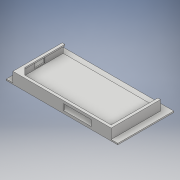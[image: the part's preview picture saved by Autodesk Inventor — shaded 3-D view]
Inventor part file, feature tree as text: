
AUTODESK INVENTOR PART (.ipt)
format: ipt  version: 2018 (Build 220112000, 112)  size: 165,888 bytes
history: native  units: mm
features: extrude x6, sketch x6, chamfer x1, projected_geometry x1
ambient origin geometry x8: Origin, YZ Plane, XZ Plane, XY Plane, X Axis, Y Axis, Z Axis, Center Point
bodies: Solid1 (feature_tree)
feature tree (14):
  extrude  "Extrusion1"  Depth=72.0mm
  extrude  "Extrusion2"  Depth=1.5mm
  extrude  "Extrusion3"  Depth=4.0mm
  extrude  "Extrusion4"  Depth=2.0mm TaperAngle=0.0deg
  extrude  "Extrusion5"  Depth=10.0mm
  extrude  "Extrusion6"  Depth=8.0mm
  chamfer  "Chamfer1"  Distance=15.0mm
  sketch  "Sketch1"  dims[d0=144.4mm d1=72.0mm]
  sketch  "Sketch2"  dims[d2=0.5mm d3=1.5mm]
  sketch  "Sketch3"  dims[d4=11.0mm d5=0.0mm d6=4.0mm]
  sketch  "Sketch4"  dims[d7=4.0mm d8=2.0mm d9=0.0mm]
  projected_geometry  "Projected Loop1"
  sketch  "Sketch5"  dims[d10=2.0mm d11=0.0mm d12=10.0mm]
  sketch  "Sketch6"  dims[d13=2.0mm d14=0.0mm d15=8.0mm d16=15.0mm d17=10.0mm d18=0.0mm d19=42.0mm d20=10.0mm d21=0.0mm d22=10.0mm d23=2.0mm d24=45.0deg]
